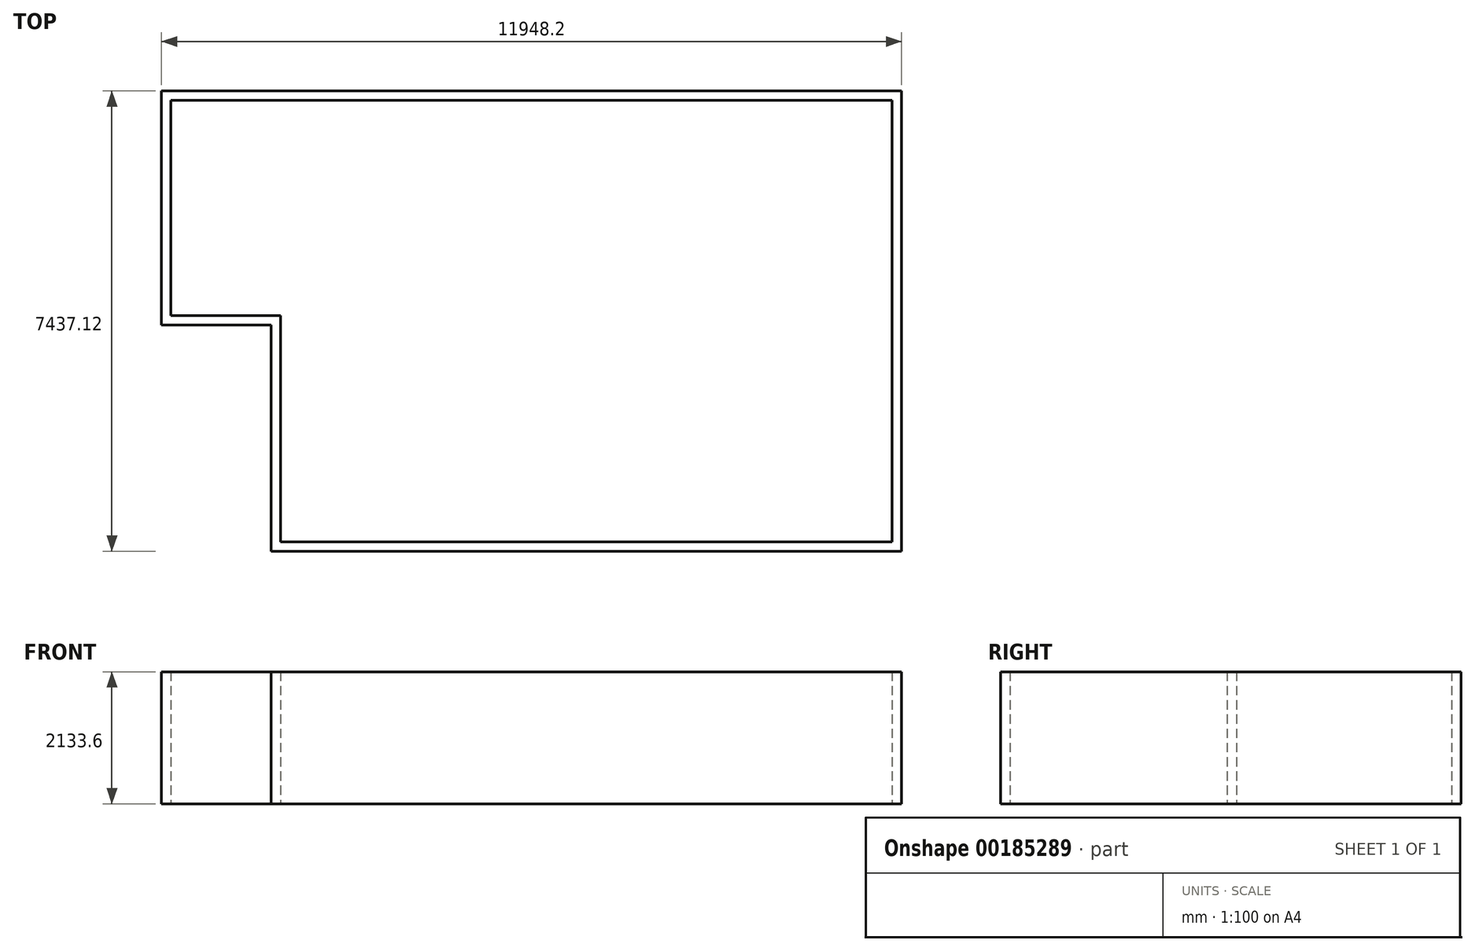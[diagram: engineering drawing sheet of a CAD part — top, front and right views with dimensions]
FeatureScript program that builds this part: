
annotation { "Feature Type Name" : "Feature", "Feature Type Description" : "" }
export const myFeature = defineFeature(function(context is Context, id is Id, definition is map)
    precondition{}
    {
        {
            var Q0;
            Q0=qCreatedBy(makeId("Top.planeOp"),FACE);
            var sketch = newSketch(context, id + "F0", { "sketchPlane" : qUnion([Q0])});
            skLineSegment(sketch, "E0.bottom", {"start": v(0, 0) * mm, "end": v(37984.18, 0) * mm, "construction": true});
            skLineSegment(sketch, "E0.top", {"start": v(0, 12237.72) * mm, "end": v(37984.18, 12237.72) * mm, "construction": true});
            skLineSegment(sketch, "E0.left", {"start": v(0, 0) * mm, "end": v(0, 12237.72) * mm, "construction": true});
            skLineSegment(sketch, "E0.right", {"start": v(37984.18, 0) * mm, "end": v(37984.18, 12237.72) * mm, "construction": true});
            skLineSegment(sketch, "E1", {"start": v(35576.26, 10317.48) * mm, "end": v(35576.26, 2880.36) * mm});
            skLineSegment(sketch, "E2", {"start": v(35576.26, 2880.36) * mm, "end": v(25395.94, 2880.36) * mm});
            skLineSegment(sketch, "E3", {"start": v(25395.94, 2880.36) * mm, "end": v(25395.94, 6537.96) * mm});
            skLineSegment(sketch, "E4", {"start": v(25395.94, 6537.96) * mm, "end": v(23628.1, 6537.96) * mm});
            skLineSegment(sketch, "E5", {"start": v(23628.1, 6537.96) * mm, "end": v(23628.1, 10317.48) * mm});
            skLineSegment(sketch, "E6", {"start": v(23628.1, 10317.48) * mm, "end": v(35576.26, 10317.48) * mm});
            skLineSegment(sketch, "E7", {"start": v(23628.1, 6537.96) * mm, "end": v(23628.1, 5059.5) * mm});
            skLineSegment(sketch, "E8", {"start": v(23628.1, 5059.5) * mm, "end": v(25395.94, 5059.5) * mm});
            skLineSegment(sketch, "E9", {"start": v(23628.1, 6537.96) * mm, "end": v(20580.1, 6537.96) * mm});
            skLineSegment(sketch, "E10", {"start": v(20580.1, 6537.96) * mm, "end": v(20580.1, 10317.48) * mm});
            skLineSegment(sketch, "E11", {"start": v(20580.1, 10317.48) * mm, "end": v(23628.1, 10317.48) * mm});
            skLineSegment(sketch, "E12.bottom", {"start": v(23190.15, 5749.05) * mm, "end": v(24194.78, 5749.05) * mm});
            skLineSegment(sketch, "E12.top", {"start": v(23190.15, 5059.5) * mm, "end": v(24194.78, 5059.5) * mm});
            skLineSegment(sketch, "E12.left", {"start": v(23190.15, 5749.05) * mm, "end": v(23190.15, 5059.5) * mm});
            skLineSegment(sketch, "E12.right", {"start": v(24194.78, 5749.05) * mm, "end": v(24194.78, 5059.5) * mm});
            skLineSegment(sketch, "E13", {"start": v(23946.84, 5749.05) * mm, "end": v(23946.84, 5059.5) * mm});
            skLineSegment(sketch, "E14", {"start": v(23719.86, 5059.5) * mm, "end": v(23719.86, 5749.05) * mm});
            skLineSegment(sketch, "E15", {"start": v(23447.42, 5059.5) * mm, "end": v(23447.42, 5749.05) * mm});
            skLineSegment(sketch, "E16", {"start": v(16780.57, 60.96) * mm, "end": v(16770.1, 3459.48) * mm});
            skLineSegment(sketch, "E17", {"start": v(16770.1, 3459.48) * mm, "end": v(21707.83, 3474.7) * mm});
            skLineSegment(sketch, "E18", {"start": v(21707.83, 3474.7) * mm, "end": v(21717.7, 274.32) * mm});
            skPoint(sketch, "E19.start.orphan", {"position": v(21707.83, 274.32) * mm});
            skLineSegment(sketch, "E20", {"start": v(16780.57, 60.96) * mm, "end": v(21717.7, 274.32) * mm});
            skLineSegment(sketch, "E21.bottom", {"start": v(20580.1, 10317.48) * mm, "end": v(16770.1, 10317.48) * mm});
            skLineSegment(sketch, "E21.top", {"start": v(20580.1, 3459.48) * mm, "end": v(16770.1, 3459.48) * mm});
            skLineSegment(sketch, "E21.left", {"start": v(20580.1, 10317.48) * mm, "end": v(20580.1, 3459.48) * mm});
            skLineSegment(sketch, "E21.right", {"start": v(16770.1, 10317.48) * mm, "end": v(16770.1, 3459.48) * mm});
            skLineSegment(sketch, "E22.0", {"start": v(25548.34, 6690.36) * mm, "end": v(23780.5, 6690.36) * mm});
            skLineSegment(sketch, "E22.1", {"start": v(23780.5, 10165.08) * mm, "end": v(35423.86, 10165.08) * mm});
            skLineSegment(sketch, "E22.2", {"start": v(35423.86, 10165.08) * mm, "end": v(35423.86, 3032.76) * mm});
            skLineSegment(sketch, "E22.3", {"start": v(23780.5, 6690.36) * mm, "end": v(23780.5, 10165.08) * mm});
            skLineSegment(sketch, "E22.4", {"start": v(35423.86, 3032.76) * mm, "end": v(25548.34, 3032.76) * mm});
            skLineSegment(sketch, "E22.5", {"start": v(25548.34, 3032.76) * mm, "end": v(25548.34, 6690.36) * mm});
            skSolve(sketch);
        }
        {
            var Q0;
            Q0=makeQuery(id+"F0.imprint","IMPRINT",FACE,{"disambiguationData":[TD([[makeQuery(id+"F0.imprint","IMPRINT",EDGE,{"derivedFrom":sQuery(id+"F0.wireOp",EDGE,"E1")}),-1.0]])]});
            extrude(context, id + "F1", {"entities" : qUnion([Q0]), "depth" : 2133.6 * mm});
        }
    });
